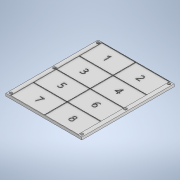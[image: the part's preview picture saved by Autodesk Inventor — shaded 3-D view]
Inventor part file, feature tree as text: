
AUTODESK INVENTOR PART (.ipt)
format: ipt  version: 2020 (Build 240168000, 168)  size: 370,688 bytes
history: native  units: in
note: dims shown in document units (in); Inventor stores cm internally (conversion verified against a paired STEP export)
features: sketch x4, extrude x3, pattern_linear x1, hole x1
ambient origin geometry x8: Origin, YZ Plane, XZ Plane, XY Plane, X Axis, Y Axis, Z Axis, Center Point
bodies: Solid1 (feature_tree)
feature tree (9):
  extrude  "Extrusion1"  Depth=13.854in
  extrude  "Extrusion4"  Depth=0.0787in
  pattern_linear  "Rectangular Pattern1"  Spacing1=0.0787in  [1 undecoded]
  hole  "Hole1"  [1 undecoded]
  extrude  "Extrusion5"  Depth=0.0787in
  sketch  "Sketch1"  dims[d0=11.4173in d1=13.854in]
  sketch  "Sketch2"  dims[d2=0.3937in d3=0.0in d4=0.0787in]
  sketch  "Sketch3"  dims[d5=0.0787in]
  sketch  "Sketch4"  dims[d6=0.0787in d7=0.0787in d8=0.0787in d13=0.0787in d14=0.0787in d17=5.03in d19=0.6195in d20=5.07in d21=3.405in d22=0.0787in d23=0.0787in d24=0.0in d25=0.7874in d27=5.1087in d28=1.5748in d30=3.4437in d31=0.375in d32=0.375in d33=0.375in d34=0.375in d35=0.375in d36=0.375in d37=0.266in d38=0.75in d39=0.438in d40=0.25in d41=0.5635in d42=0.3898in d43=0.0in d44=0.0787in d45=0.0in]
note: 2 required parameter values undecoded (feature->parameter linkage not recoverable at this tier; creation-order binding heuristic only, values carry confidence <= 0.55)
